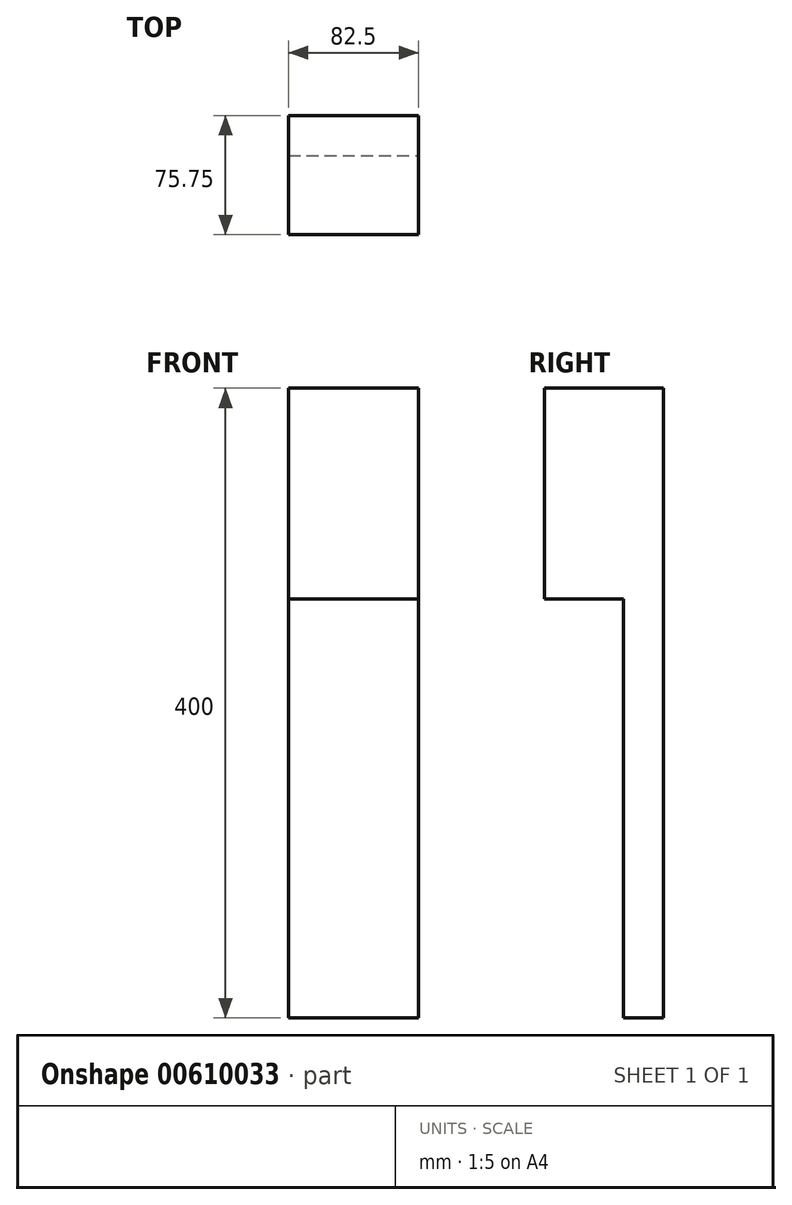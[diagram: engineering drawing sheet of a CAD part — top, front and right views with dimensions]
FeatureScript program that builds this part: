
annotation { "Feature Type Name" : "Feature", "Feature Type Description" : "" }
export const myFeature = defineFeature(function(context is Context, id is Id, definition is map)
    precondition{}
    {
        {
            var Q0;
            Q0=qCreatedBy(makeId("Top.planeOp"),FACE);
            var sketch = newSketch(context, id + "F0", { "sketchPlane" : qUnion([Q0])});
            skLineSegment(sketch, "E0.bottom", {"start": v(41.25, -12.7) * mm, "end": v(-41.25, -12.7) * mm});
            skLineSegment(sketch, "E0.top", {"start": v(41.25, 12.7) * mm, "end": v(-41.25, 12.7) * mm});
            skLineSegment(sketch, "E0.left", {"start": v(41.25, -12.7) * mm, "end": v(41.25, 12.7) * mm});
            skLineSegment(sketch, "E0.right", {"start": v(-41.25, -12.7) * mm, "end": v(-41.25, 12.7) * mm});
            skPoint(sketch, "E0.middle", {"position": v(0, 0) * mm});
            skSolve(sketch);
        }
        {
            var Q0;
            Q0=makeQuery(id+"F0.imprint","IMPRINT",FACE,{"disambiguationData":[TD([[makeQuery(id+"F0.imprint","IMPRINT",EDGE,{"derivedFrom":sQuery(id+"F0.wireOp",EDGE,"E0.bottom")}),-1.0]])]});
            extrude(context, id + "F1", {"entities" : qUnion([Q0]), "depth" : 200 * mm, "offsetDistance" : 25 * mm});
        }
        {
            var Q0;
            Q0=makeQuery(id+"F1.opExtrude","SWEPT_FACE",FACE,{"disambiguationData":[OSD([sQuery(id+"F0.wireOp",EDGE,"E0.bottom")])]});
            var sketch = newSketch(context, id + "F2", { "sketchPlane" : qUnion([Q0])});
            skLineSegment(sketch, "E1.bottom", {"start": v(-41.25, 200) * mm, "end": v(41.25, 200) * mm});
            skLineSegment(sketch, "E1.top", {"start": v(-41.25, 66) * mm, "end": v(41.25, 66) * mm});
            skLineSegment(sketch, "E1.left", {"start": v(-41.25, 200) * mm, "end": v(-41.25, 66) * mm});
            skLineSegment(sketch, "E1.right", {"start": v(41.25, 200) * mm, "end": v(41.25, 66) * mm});
            skSolve(sketch);
        }
        {
            var Q0;
            Q0=makeQuery(id+"F2.imprint","IMPRINT",FACE,{"disambiguationData":[TD([[makeQuery(id+"F2.imprint","IMPRINT",EDGE,{"derivedFrom":sQuery(id+"F2.wireOp",EDGE,"E1.bottom")}),1.0]])]});
            extrude(context, id + "F3", {"entities" : qUnion([Q0]), "operationType" : NewBodyOperationType.ADD, "depth" : 50.35 * mm, "offsetDistance" : 25 * mm});
        }
        {
            var Q0;
            Q0=makeQuery(id+"F1.opExtrude","CAP_FACE",FACE,{"disambiguationData":[OSD([sQuery(id+"F0.wireOp",EDGE,"E0.bottom"),sQuery(id+"F0.wireOp",EDGE,"E0.top"),sQuery(id+"F0.wireOp",EDGE,"E0.left"),sQuery(id+"F0.wireOp",EDGE,"E0.right")])],"isStart":true});
            extrude(context, id + "F4", {"entities" : qUnion([Q0]), "operationType" : NewBodyOperationType.ADD, "depth" : 200 * mm, "offsetDistance" : 25 * mm});
        }
    });
